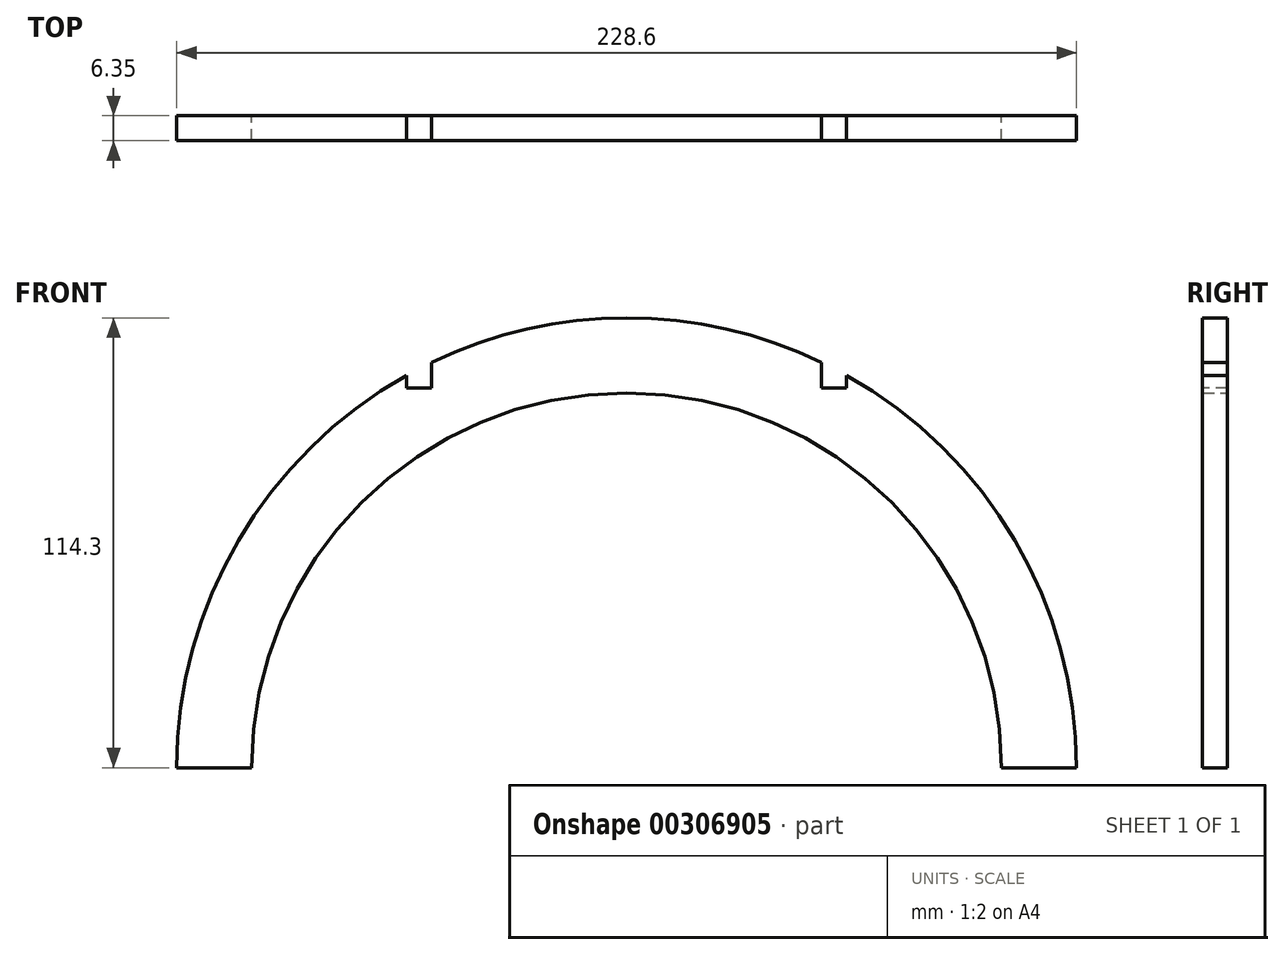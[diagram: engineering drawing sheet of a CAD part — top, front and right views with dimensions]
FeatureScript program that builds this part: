
annotation { "Feature Type Name" : "Feature", "Feature Type Description" : "" }
export const myFeature = defineFeature(function(context is Context, id is Id, definition is map)
    precondition{}
    {
        {
            var Q0;
            Q0=qCreatedBy(makeId("Front.planeOp"),FACE);
            var sketch = newSketch(context, id + "F0", { "sketchPlane" : qUnion([Q0])});
            skArc(sketch, "E0", {"start": v(114.3, 0) * mm, "mid": v(80.82, 80.82) * mm, "end": v(0, 114.3) * mm});
            skPoint(sketch, "E1.orphan", {"position": v(-126.25, 0) * mm});
            skArc(sketch, "E2.MirrorCS", {"start": v(-114.3, 0) * mm, "mid": v(-80.82, 80.82) * mm, "end": v(0, 114.3) * mm});
            skLineSegment(sketch, "E3", {"start": v(-114.3, 0) * mm, "end": v(-95.25, 0) * mm});
            skPoint(sketch, "E4.end.orphan", {"position": v(110.5, 0) * mm});
            skLineSegment(sketch, "E5", {"start": v(114.3, 0) * mm, "end": v(95.25, 0) * mm});
            skArc(sketch, "E6", {"start": v(95.25, 0) * mm, "mid": v(0, 95.25) * mm, "end": v(-95.25, 0) * mm});
            skSolve(sketch);
        }
        {
            var Q0;
            Q0 = qSketchRegion(id + "F0", true);
            extrude(context, id + "F1", {"entities" : qUnion([Q0]), "depth" : 6.35 * mm});
        }
        {
            var Q0;
            Q0=qCreatedBy(makeId("Top.planeOp"),FACE);
            cPlane(context, id + "F2", {"entities" : qUnion([Q0]), "cplaneType" : CPlaneType.OFFSET, "offset" : 114.3 * mm, "width" : 152.4 * mm, "height" : 152.4 * mm});
        }
        {
            var Q0;
            Q0=qCreatedBy(id+"F2.planeOp",FACE);
            var sketch = newSketch(context, id + "F3", { "sketchPlane" : qUnion([Q0])});
            skLineSegment(sketch, "E7.bottom", {"start": v(-55.88, 0) * mm, "end": v(-49.53, 0) * mm});
            skLineSegment(sketch, "E7.top", {"start": v(-55.88, -6.35) * mm, "end": v(-49.53, -6.35) * mm});
            skLineSegment(sketch, "E7.left", {"start": v(-55.88, 0) * mm, "end": v(-55.88, -6.35) * mm});
            skLineSegment(sketch, "E7.right", {"start": v(-49.53, 0) * mm, "end": v(-49.53, -6.35) * mm});
            skLineSegment(sketch, "E8.MirrorCS", {"start": v(55.88, 0) * mm, "end": v(55.88, -6.35) * mm});
            skLineSegment(sketch, "E9.MirrorCS", {"start": v(55.88, 0) * mm, "end": v(49.53, 0) * mm});
            skLineSegment(sketch, "E10.MirrorCS", {"start": v(49.53, 0) * mm, "end": v(49.53, -6.35) * mm});
            skLineSegment(sketch, "E11.MirrorCS", {"start": v(55.88, -6.35) * mm, "end": v(49.53, -6.35) * mm});
            skSolve(sketch);
        }
        {
            var Q0;
            Q0 = qSketchRegion(id + "F3", true);
            extrude(context, id + "F4", {"entities" : qUnion([Q0]), "operationType" : NewBodyOperationType.REMOVE, "oppositeDirection" : true, "depth" : 17.78 * mm});
        }
    });
